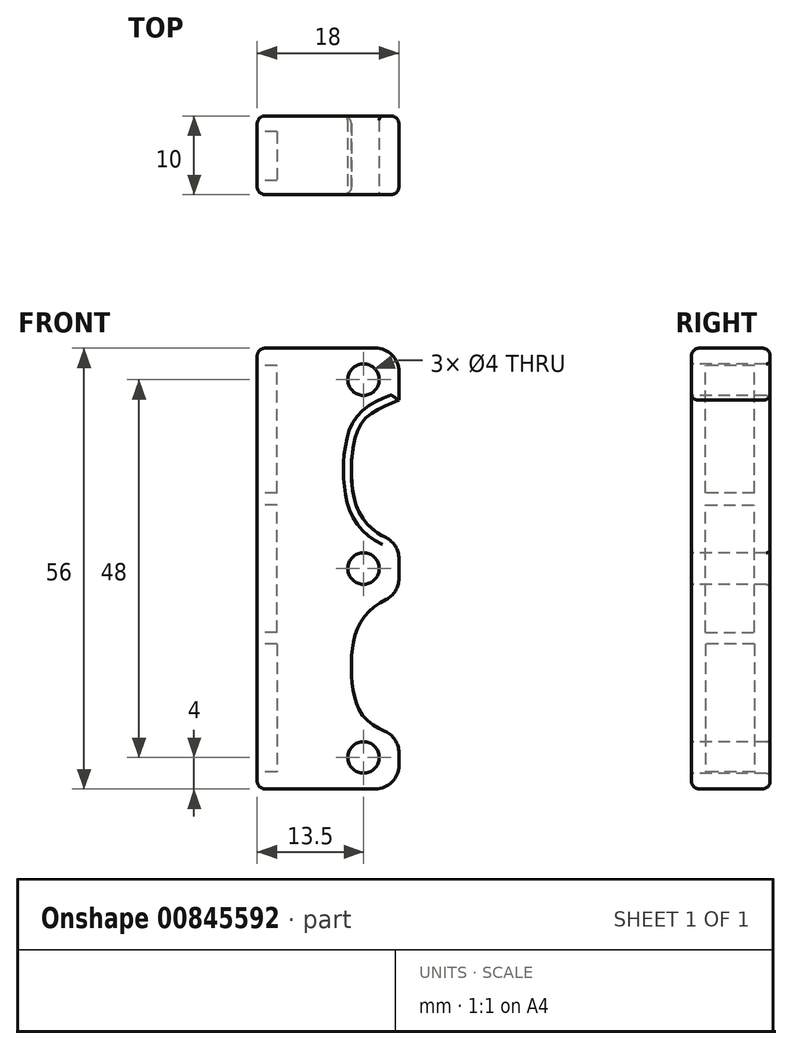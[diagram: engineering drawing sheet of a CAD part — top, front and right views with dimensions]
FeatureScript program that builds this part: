
annotation { "Feature Type Name" : "Feature", "Feature Type Description" : "" }
export const myFeature = defineFeature(function(context is Context, id is Id, definition is map)
    precondition{}
    {
        {
            var Q0;
            Q0=qCreatedBy(makeId("Front.planeOp"),FACE);
            var sketch = newSketch(context, id + "F0", { "sketchPlane" : qUnion([Q0])});
            skLineSegment(sketch, "E0.bottom", {"start": v(0, 28) * mm, "end": v(18, 28) * mm});
            skLineSegment(sketch, "E0.top", {"start": v(0, -28) * mm, "end": v(18, -28) * mm});
            skLineSegment(sketch, "E0.left", {"start": v(0, 28) * mm, "end": v(0, -28) * mm});
            skLineSegment(sketch, "E0.right", {"start": v(18, 28) * mm, "end": v(18, -28) * mm});
            skSolve(sketch);
        }
        {
            var Q0;
            Q0=qSketchRegion(id+"F0",true);
            extrude(context, id + "F1", {"entities" : qUnion([Q0]), "depth" : 10 * mm, "offsetDistance" : 25 * mm});
        }
        {
            var Q0;
            Q0=makeQuery(id+"F1.opExtrude","CAP_FACE",FACE,{"disambiguationData":[OSD([sQuery(id+"F0.wireOp",EDGE,"E0.bottom"),sQuery(id+"F0.wireOp",EDGE,"E0.top"),sQuery(id+"F0.wireOp",EDGE,"E0.left"),sQuery(id+"F0.wireOp",EDGE,"E0.right")])],"isStart":false});
            var sketch = newSketch(context, id + "F2", { "sketchPlane" : qUnion([Q0])});
            skCircle(sketch, "E1", {"center": v(13.5, 0) * mm, "radius": 2 * mm});
            skCircle(sketch, "E2", {"center": v(13.5, -24) * mm, "radius": 2 * mm});
            skCircle(sketch, "E3", {"center": v(13.5, 24) * mm, "radius": 2 * mm});
            skLineSegment(sketch, "E4", {"start": v(13.5, 24) * mm, "end": v(13.5, -24) * mm, "construction": true});
            skSolve(sketch);
        }
        {
            var Q0;
            Q0=qSketchRegion(id+"F2",true);
            extrude(context, id + "F3", {"entities" : qUnion([Q0]), "operationType" : NewBodyOperationType.REMOVE, "oppositeDirection" : true, "depth" : 25 * mm, "offsetDistance" : 25 * mm});
        }
        {
            var Q0;
            Q0=makeQuery(id+"F1.opExtrude","SWEPT_EDGE",EDGE,{"disambiguationData":[OSD([sQuery(id+"F0.wireOp",EDGE,"E0.bottom"),sQuery(id+"F0.wireOp",EDGE,"E0.right")])]});
            var Q1;
            Q1=makeQuery(id+"F1.opExtrude","SWEPT_EDGE",EDGE,{"disambiguationData":[OSD([sQuery(id+"F0.wireOp",EDGE,"E0.top"),sQuery(id+"F0.wireOp",EDGE,"E0.right")])]});
            fillet(context, id + "F4", {"entities" : qUnion([Q0, Q1]), "radius" : 3 * mm, "tangentPropagation" : true, "allowEdgeOverflow" : false});
        }
        {
            var Q0;
            Q0=makeQuery(id+"F1.opExtrude","CAP_FACE",FACE,{"disambiguationData":[OSD([sQuery(id+"F0.wireOp",EDGE,"E0.bottom"),sQuery(id+"F0.wireOp",EDGE,"E0.top"),sQuery(id+"F0.wireOp",EDGE,"E0.left"),sQuery(id+"F0.wireOp",EDGE,"E0.right")])],"isStart":false});
            var sketch = newSketch(context, id + "F5", { "sketchPlane" : qUnion([Q0])});
            skFitSpline(sketch, "E5", {"points": [v(18, 21.38) * mm, v(12.51, 16.82) * mm, v(12.56, 8.11) * mm, v(18, 3.24) * mm], "startDerivative": vector(-35.06, -13.2) * mm, "endDerivative": vector(28.08, -10.18) * mm});
            skFitSpline(sketch, "E6.MirrorCS", {"points": [v(18, -21.38) * mm, v(12.51, -16.82) * mm, v(12.56, -8.11) * mm, v(18, -3.24) * mm], "startDerivative": vector(-35.06, 13.2) * mm, "endDerivative": vector(28.08, 10.18) * mm});
            skLineSegment(sketch, "E7", {"start": v(18, 21.38) * mm, "end": v(18, 3.24) * mm});
            skLineSegment(sketch, "E8", {"start": v(18, -3.24) * mm, "end": v(18, -21.38) * mm});
            skSolve(sketch);
        }
        {
            var Q0;
            Q0=qSketchRegion(id+"F5",true);
            extrude(context, id + "F6", {"entities" : qUnion([Q0]), "operationType" : NewBodyOperationType.REMOVE, "oppositeDirection" : true, "depth" : 25 * mm, "offsetDistance" : 25 * mm});
        }
        {
            var Q0;
            {var subQ0=sQuery(id+"F5.wireOp",EDGE,"E7");var subQ1=sQuery(id+"F5.wireOp",EDGE,"E5");var subQ2=sQuery(id+"F0.wireOp",EDGE,"E0.right");Q0=makeQuery(id+"F6.boolean.opBoolean","COPY",EDGE,{"derivedFrom":makeQuery(id+"F6.opExtrude","SWEPT_EDGE",EDGE,{"disambiguationData":[OSD([subQ2,subQ1,subQ0]),TDD([makeQuery(id+"F5.imprint","INTERSECT",VERTEX,{"disambiguationData":[OD(0.0)],"derivedFrom":[makeQuery(id+"F1.opExtrude","CAP_EDGE",EDGE,{"disambiguationData":[OSD([subQ2])],"isStart":false}),subQ1,subQ0]})])]})});}
            var Q1;
            {var subQ0=sQuery(id+"F5.wireOp",EDGE,"E8");var subQ1=sQuery(id+"F5.wireOp",EDGE,"E6.MirrorCS");var subQ2=sQuery(id+"F0.wireOp",EDGE,"E0.right");Q1=makeQuery(id+"F6.boolean.opBoolean","COPY",EDGE,{"derivedFrom":makeQuery(id+"F6.opExtrude","SWEPT_EDGE",EDGE,{"disambiguationData":[OSD([subQ2,subQ1,subQ0]),TDD([makeQuery(id+"F5.imprint","INTERSECT",VERTEX,{"disambiguationData":[OD(1.0)],"derivedFrom":[makeQuery(id+"F1.opExtrude","CAP_EDGE",EDGE,{"disambiguationData":[OSD([subQ2])],"isStart":false}),subQ1,subQ0]})])]})});}
            var Q2;
            {var subQ0=sQuery(id+"F5.wireOp",EDGE,"E7");var subQ1=sQuery(id+"F5.wireOp",EDGE,"E5");var subQ2=sQuery(id+"F0.wireOp",EDGE,"E0.right");Q2=makeQuery(id+"F6.boolean.opBoolean","COPY",EDGE,{"derivedFrom":makeQuery(id+"F6.opExtrude","SWEPT_EDGE",EDGE,{"disambiguationData":[OSD([subQ2,subQ1,subQ0]),TDD([makeQuery(id+"F5.imprint","INTERSECT",VERTEX,{"disambiguationData":[OD(1.0)],"derivedFrom":[makeQuery(id+"F1.opExtrude","CAP_EDGE",EDGE,{"disambiguationData":[OSD([subQ2])],"isStart":false}),subQ1,subQ0]})])]})});}
            var Q3;
            {var subQ0=sQuery(id+"F5.wireOp",EDGE,"E8");var subQ1=sQuery(id+"F5.wireOp",EDGE,"E6.MirrorCS");var subQ2=sQuery(id+"F0.wireOp",EDGE,"E0.right");Q3=makeQuery(id+"F6.boolean.opBoolean","COPY",EDGE,{"derivedFrom":makeQuery(id+"F6.opExtrude","SWEPT_EDGE",EDGE,{"disambiguationData":[OSD([subQ2,subQ1,subQ0]),TDD([makeQuery(id+"F5.imprint","INTERSECT",VERTEX,{"disambiguationData":[OD(0.0)],"derivedFrom":[makeQuery(id+"F1.opExtrude","CAP_EDGE",EDGE,{"disambiguationData":[OSD([subQ2])],"isStart":false}),subQ1,subQ0]})])]})});}
            fillet(context, id + "F7", {"entities" : qUnion([Q0, Q1, Q2, Q3]), "radius" : 3 * mm, "tangentPropagation" : true, "allowEdgeOverflow" : false});
        }
        {
            var Q0;
            Q0=makeQuery(id+"F1.opExtrude","SWEPT_EDGE",EDGE,{"disambiguationData":[OSD([sQuery(id+"F0.wireOp",EDGE,"E0.top"),sQuery(id+"F0.wireOp",EDGE,"E0.left")])]});
            var Q1;
            Q1=makeQuery(id+"F1.opExtrude","SWEPT_EDGE",EDGE,{"disambiguationData":[OSD([sQuery(id+"F0.wireOp",EDGE,"E0.bottom"),sQuery(id+"F0.wireOp",EDGE,"E0.left")])]});
            fillet(context, id + "F8", {"entities" : qUnion([Q0, Q1]), "radius" : 1 * mm, "tangentPropagation" : true, "allowEdgeOverflow" : false});
        }
        {
            var Q0;
            Q0=makeQuery(id+"F1.opExtrude","SWEPT_FACE",FACE,{"disambiguationData":[OSD([sQuery(id+"F0.wireOp",EDGE,"E0.left")])]});
            var sketch = newSketch(context, id + "F9", { "sketchPlane" : qUnion([Q0])});
            skLineSegment(sketch, "E9.bottom", {"start": v(2, -9.6) * mm, "end": v(8.2, -9.6) * mm});
            skLineSegment(sketch, "E9.top", {"start": v(2, -25.8) * mm, "end": v(8.2, -25.8) * mm});
            skLineSegment(sketch, "E9.left", {"start": v(2, -9.6) * mm, "end": v(2, -25.8) * mm});
            skLineSegment(sketch, "E9.right", {"start": v(8.2, -9.6) * mm, "end": v(8.2, -25.8) * mm});
            skLineSegment(sketch, "E10.bottom", {"start": v(8.2, -8.1) * mm, "end": v(2, -8.1) * mm});
            skLineSegment(sketch, "E10.top", {"start": v(8.2, 8.1) * mm, "end": v(2, 8.1) * mm});
            skLineSegment(sketch, "E10.left", {"start": v(8.2, -8.1) * mm, "end": v(8.2, 8.1) * mm});
            skLineSegment(sketch, "E10.right", {"start": v(2, -8.1) * mm, "end": v(2, 8.1) * mm});
            skLineSegment(sketch, "E11.MirrorCS", {"start": v(2, 9.6) * mm, "end": v(8.2, 9.6) * mm});
            skLineSegment(sketch, "E12.MirrorCS", {"start": v(2, 9.6) * mm, "end": v(2, 25.8) * mm});
            skLineSegment(sketch, "E13.MirrorCS", {"start": v(2, 25.8) * mm, "end": v(8.2, 25.8) * mm});
            skLineSegment(sketch, "E14.MirrorCS", {"start": v(8.2, 9.6) * mm, "end": v(8.2, 25.8) * mm});
            skSolve(sketch);
        }
        {
            var Q0;
            Q0=qSketchRegion(id+"F9",true);
            extrude(context, id + "F10", {"entities" : qUnion([Q0]), "operationType" : NewBodyOperationType.REMOVE, "oppositeDirection" : true, "depth" : 2.5 * mm, "offsetDistance" : 25 * mm});
        }
        {
            var Q0;
            Q0=makeQuery(id+"F1.opExtrude","CAP_EDGE",EDGE,{"disambiguationData":[OSD([sQuery(id+"F0.wireOp",EDGE,"E0.bottom")])],"isStart":false});
            var Q1;
            Q1=makeQuery(id+"F1.opExtrude","CAP_EDGE",EDGE,{"disambiguationData":[OSD([sQuery(id+"F0.wireOp",EDGE,"E0.left")])],"isStart":true});
            fillet(context, id + "F11", {"entities" : qUnion([Q0, Q1]), "radius" : 1 * mm, "tangentPropagation" : true, "allowEdgeOverflow" : false});
        }
        {
            var Q0;
            Q0=makeQuery(id+"F3.boolean.opBoolean","COPY",EDGE,{"derivedFrom":makeQuery(id+"F3.opExtrude","CAP_EDGE",EDGE,{"disambiguationData":[OSD([sQuery(id+"F2.wireOp",EDGE,"E2")])],"isStart":true})});
            var Q1;
            Q1=makeQuery(id+"F3.boolean.opBoolean","COPY",EDGE,{"derivedFrom":makeQuery(id+"F3.opExtrude","CAP_EDGE",EDGE,{"disambiguationData":[OSD([sQuery(id+"F2.wireOp",EDGE,"E1")])],"isStart":true})});
            var Q2;
            Q2=makeQuery(id+"F3.boolean.opBoolean","COPY",EDGE,{"derivedFrom":makeQuery(id+"F3.opExtrude","CAP_EDGE",EDGE,{"disambiguationData":[OSD([sQuery(id+"F2.wireOp",EDGE,"E3")])],"isStart":true})});
            var Q3;
            Q3=makeQuery(id+"F3.boolean.opBoolean","INTERSECT",EDGE,{"derivedFrom":[makeQuery(id+"F1.opExtrude","CAP_FACE",FACE,{"disambiguationData":[OSD([sQuery(id+"F0.wireOp",EDGE,"E0.bottom"),sQuery(id+"F0.wireOp",EDGE,"E0.top"),sQuery(id+"F0.wireOp",EDGE,"E0.left"),sQuery(id+"F0.wireOp",EDGE,"E0.right")])],"isStart":true}),makeQuery(id+"F3.opExtrude","SWEPT_FACE",FACE,{"disambiguationData":[OSD([sQuery(id+"F2.wireOp",EDGE,"E3")])]})]});
            var Q4;
            Q4=makeQuery(id+"F3.boolean.opBoolean","INTERSECT",EDGE,{"derivedFrom":[makeQuery(id+"F1.opExtrude","CAP_FACE",FACE,{"disambiguationData":[OSD([sQuery(id+"F0.wireOp",EDGE,"E0.bottom"),sQuery(id+"F0.wireOp",EDGE,"E0.top"),sQuery(id+"F0.wireOp",EDGE,"E0.left"),sQuery(id+"F0.wireOp",EDGE,"E0.right")])],"isStart":true}),makeQuery(id+"F3.opExtrude","SWEPT_FACE",FACE,{"disambiguationData":[OSD([sQuery(id+"F2.wireOp",EDGE,"E1")])]})]});
            var Q5;
            Q5=makeQuery(id+"F3.boolean.opBoolean","INTERSECT",EDGE,{"derivedFrom":[makeQuery(id+"F1.opExtrude","CAP_FACE",FACE,{"disambiguationData":[OSD([sQuery(id+"F0.wireOp",EDGE,"E0.bottom"),sQuery(id+"F0.wireOp",EDGE,"E0.top"),sQuery(id+"F0.wireOp",EDGE,"E0.left"),sQuery(id+"F0.wireOp",EDGE,"E0.right")])],"isStart":true}),makeQuery(id+"F3.opExtrude","SWEPT_FACE",FACE,{"disambiguationData":[OSD([sQuery(id+"F2.wireOp",EDGE,"E2")])]})]});
            fillet(context, id + "F12", {"entities" : qUnion([Q0, Q1, Q2, Q3, Q4, Q5]), "radius" : 0.5 * mm, "tangentPropagation" : true, "allowEdgeOverflow" : false});
        }
        {
            var Q0;
            Q0=makeQuery(id+"F1.opExtrude","SWEPT_FACE",FACE,{"disambiguationData":[OSD([sQuery(id+"F0.wireOp",EDGE,"E0.left")])]});
            var sketch = newSketch(context, id + "F13", { "sketchPlane" : qUnion([Q0])});
            skLineSegment(sketch, "E15.bottom", {"start": v(3, 24.8) * mm, "end": v(7.2, 24.8) * mm});
            skLineSegment(sketch, "E15.top", {"start": v(3, 10.6) * mm, "end": v(7.2, 10.6) * mm});
            skLineSegment(sketch, "E15.left", {"start": v(3, 24.8) * mm, "end": v(3, 10.6) * mm});
            skLineSegment(sketch, "E15.right", {"start": v(7.2, 24.8) * mm, "end": v(7.2, 10.6) * mm});
            skLineSegment(sketch, "E16.bottom", {"start": v(3, 7.1) * mm, "end": v(7.2, 7.1) * mm});
            skLineSegment(sketch, "E16.top", {"start": v(3, -7.1) * mm, "end": v(7.2, -7.1) * mm});
            skLineSegment(sketch, "E16.left", {"start": v(3, 7.1) * mm, "end": v(3, -7.1) * mm});
            skLineSegment(sketch, "E16.right", {"start": v(7.2, 7.1) * mm, "end": v(7.2, -7.1) * mm});
            skLineSegment(sketch, "E17.bottom", {"start": v(3, -10.6) * mm, "end": v(7.2, -10.6) * mm});
            skLineSegment(sketch, "E17.top", {"start": v(3, -24.8) * mm, "end": v(7.2, -24.8) * mm});
            skLineSegment(sketch, "E17.left", {"start": v(3, -10.6) * mm, "end": v(3, -24.8) * mm});
            skLineSegment(sketch, "E17.right", {"start": v(7.2, -10.6) * mm, "end": v(7.2, -24.8) * mm});
            skSolve(sketch);
        }
        {
            var Q0;
            Q0=qSketchRegion(id+"F13",true);
            extrude(context, id + "F14", {"entities" : qUnion([Q0]), "operationType" : NewBodyOperationType.REMOVE, "endBound" : BoundingType.UP_TO_NEXT, "oppositeDirection" : true, "depth" : 25 * mm, "offsetDistance" : 25 * mm});
        }
    });
